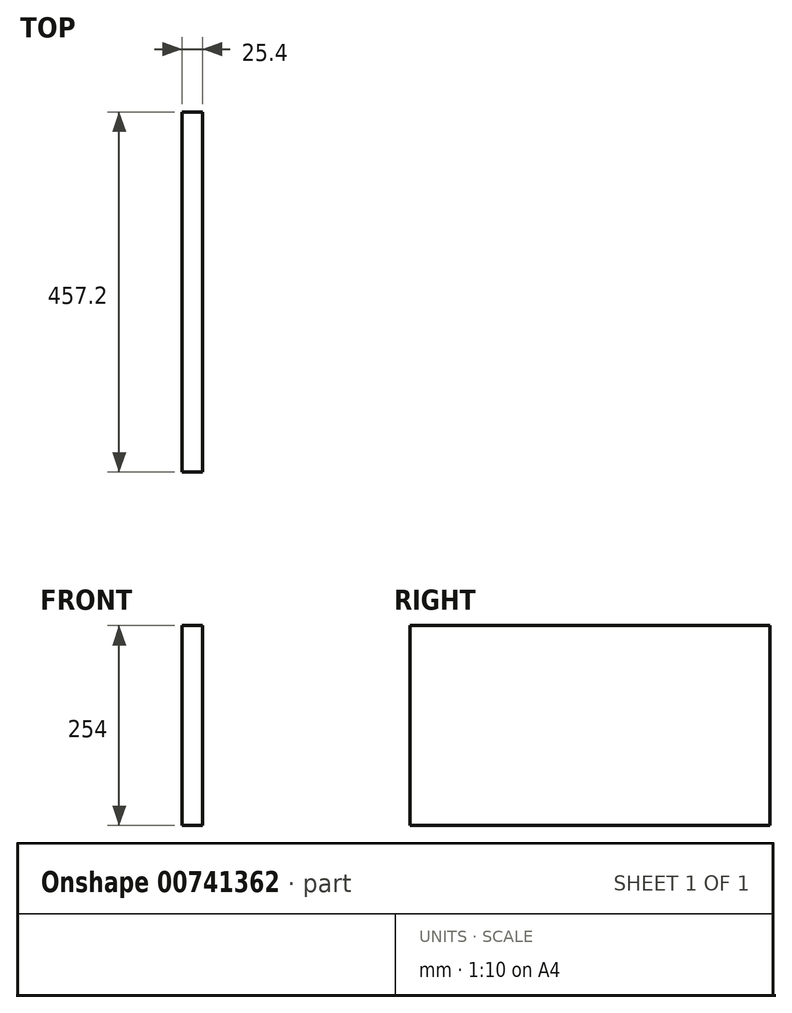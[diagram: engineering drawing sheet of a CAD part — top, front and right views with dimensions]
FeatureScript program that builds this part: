
annotation { "Feature Type Name" : "Feature", "Feature Type Description" : "" }
export const myFeature = defineFeature(function(context is Context, id is Id, definition is map)
    precondition{}
    {
        {
            var Q0;
            Q0=qCreatedBy(makeId("Right.planeOp"),FACE);
            var sketch = newSketch(context, id + "F0", { "sketchPlane" : qUnion([Q0])});
            skLineSegment(sketch, "E0.bottom", {"start": v(-228.6, 127) * mm, "end": v(228.6, 127) * mm});
            skLineSegment(sketch, "E0.top", {"start": v(-228.6, -127) * mm, "end": v(228.6, -127) * mm});
            skLineSegment(sketch, "E0.left", {"start": v(-228.6, 127) * mm, "end": v(-228.6, -127) * mm});
            skLineSegment(sketch, "E0.right", {"start": v(228.6, 127) * mm, "end": v(228.6, -127) * mm});
            skPoint(sketch, "E0.middle", {"position": v(0, 0) * mm});
            skSolve(sketch);
        }
        {
            var Q0;
            Q0=makeQuery(id+"F0.imprint","IMPRINT",FACE,{"disambiguationData":[TD([[makeQuery(id+"F0.imprint","IMPRINT",EDGE,{"derivedFrom":sQuery(id+"F0.wireOp",EDGE,"E0.bottom")}),-1.0]])]});
            extrude(context, id + "F1", {"entities" : qUnion([Q0]), "depth" : 25.4 * mm, "offsetDistance" : 25.4 * mm});
        }
    });
